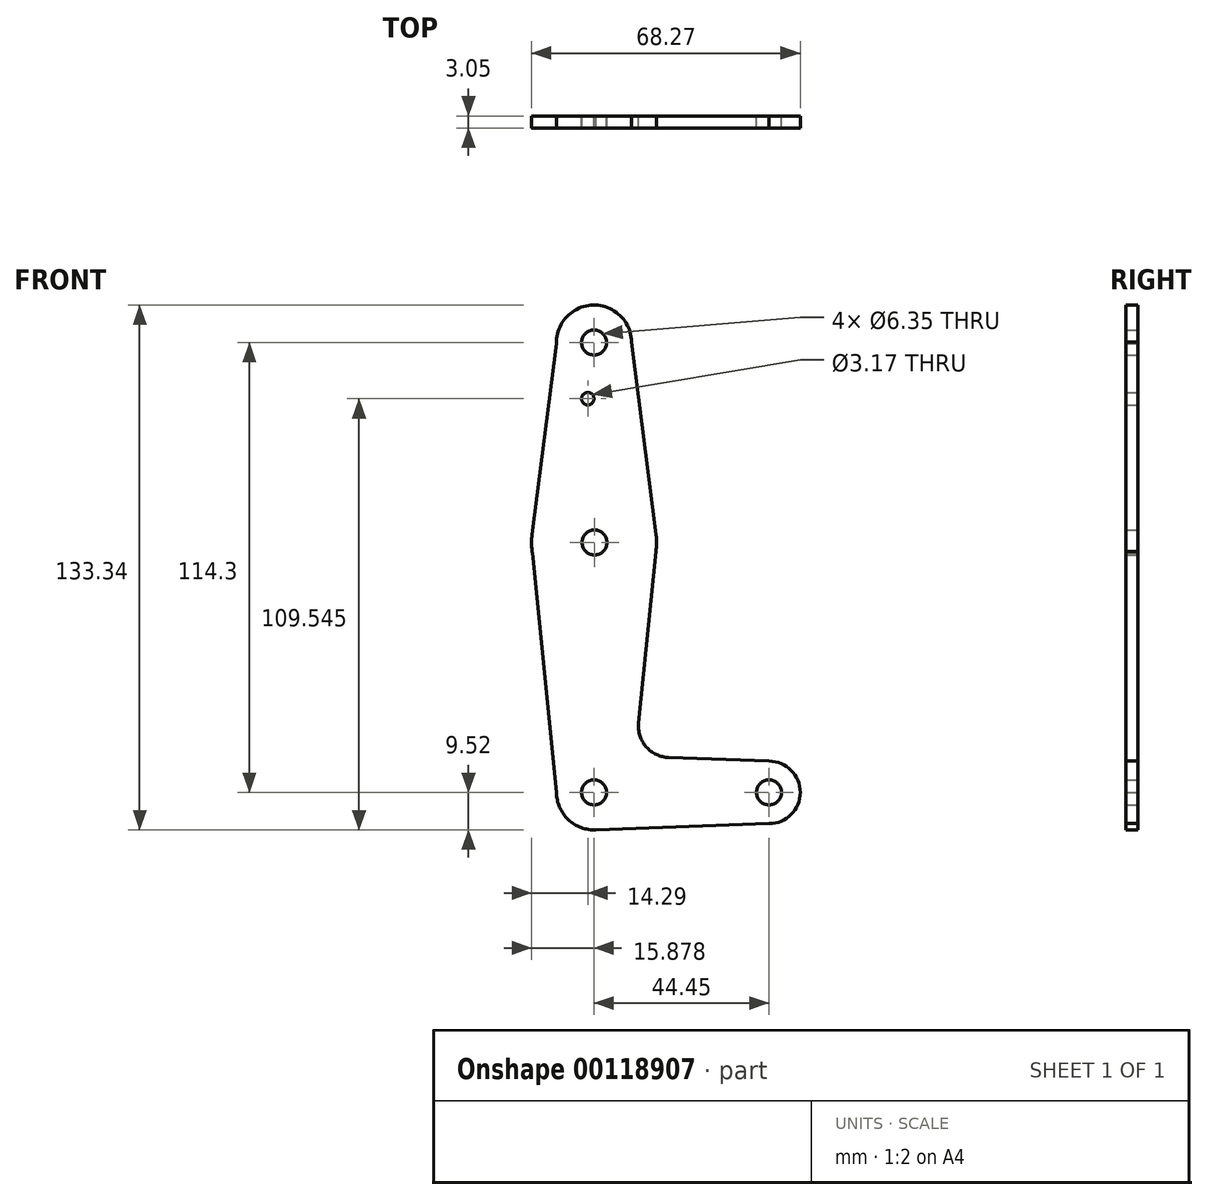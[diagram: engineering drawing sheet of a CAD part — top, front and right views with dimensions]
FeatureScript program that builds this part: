
annotation { "Feature Type Name" : "Feature", "Feature Type Description" : "" }
export const myFeature = defineFeature(function(context is Context, id is Id, definition is map)
    precondition{}
    {
        {
            var Q0;
            Q0=qCreatedBy(makeId("Front.planeOp"),FACE);
            var sketch = newSketch(context, id + "F0", { "sketchPlane" : qUnion([Q0])});
            skLineSegment(sketch, "E0", {"start": v(-0.12, 50.8) * mm, "end": v(-0.12, -63.5) * mm, "construction": true});
            skLineSegment(sketch, "E1", {"start": v(-0.12, -63.5) * mm, "end": v(44.33, -63.5) * mm, "construction": true});
            skCircle(sketch, "E2", {"center": v(-0.12, 50.8) * mm, "radius": 9.53 * mm});
            skCircle(sketch, "E3", {"center": v(-0.12, 0) * mm, "radius": 15.88 * mm});
            skCircle(sketch, "E4", {"center": v(-0.12, -63.5) * mm, "radius": 9.53 * mm});
            skCircle(sketch, "E5", {"center": v(44.33, -63.5) * mm, "radius": 7.94 * mm});
            skCircle(sketch, "E6", {"center": v(-0.12, 50.8) * mm, "radius": 3.18 * mm});
            skLineSegment(sketch, "E7", {"start": v(9.4, 50.95) * mm, "end": v(15.88, 0) * mm});
            skLineSegment(sketch, "E8", {"start": v(15.6, -2.23) * mm, "end": v(11.21, -45.91) * mm});
            skLineSegment(sketch, "E9", {"start": v(-9.64, 50.5) * mm, "end": v(-16.13, 0) * mm});
            skLineSegment(sketch, "E10", {"start": v(-15.77, -2.67) * mm, "end": v(-9.65, -63.5) * mm});
            skLineSegment(sketch, "E11", {"start": v(0, -73.02) * mm, "end": v(44.33, -71.44) * mm});
            skLineSegment(sketch, "E12", {"start": v(18.84, -54.65) * mm, "end": v(44.33, -55.56) * mm});
            skCircle(sketch, "E13", {"center": v(-1.7, 36.53) * mm, "radius": 1.59 * mm});
            skCircle(sketch, "E14", {"center": v(0, 0) * mm, "radius": 3.18 * mm});
            skCircle(sketch, "E15", {"center": v(-0.12, -63.5) * mm, "radius": 3.18 * mm});
            skPoint(sketch, "E16.newPointB", {"position": v(0, -53.98) * mm});
            skArc(sketch, "E16.filletArc", {"start": v(11.21, -45.91) * mm, "mid": v(13.14, -51.93) * mm, "end": v(18.84, -54.65) * mm});
            skCircle(sketch, "E17", {"center": v(44.33, -63.5) * mm, "radius": 3.18 * mm});
            skSolve(sketch);
        }
        {
            var Q0;
            Q0 = qSketchRegion(id + "F0", true);
            extrude(context, id + "F1", {"entities" : qUnion([Q0]), "depth" : 3.05 * mm});
        }
    });
